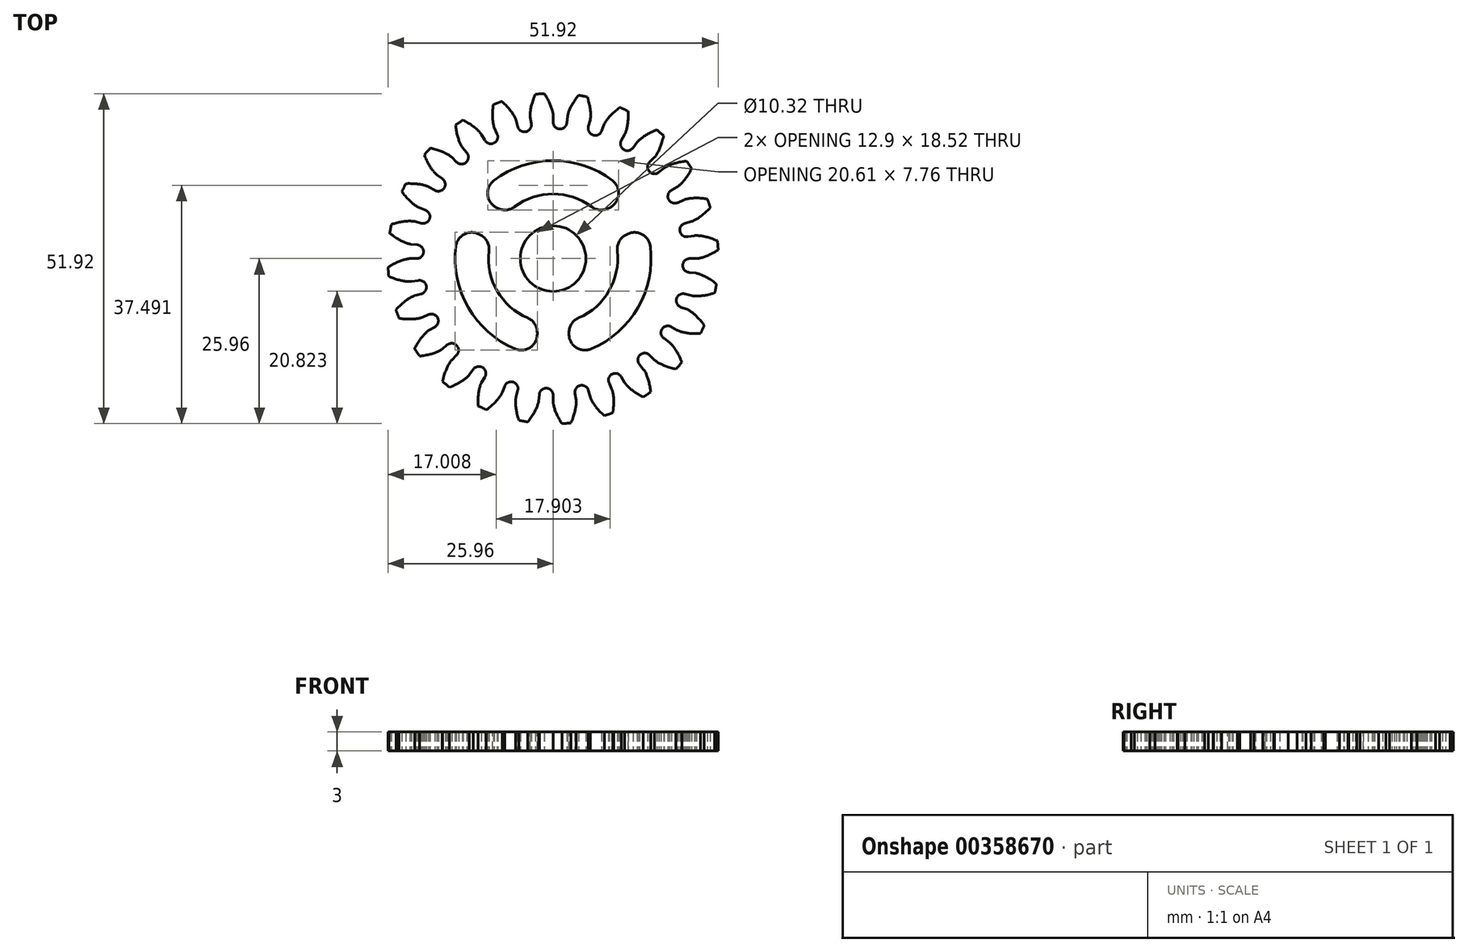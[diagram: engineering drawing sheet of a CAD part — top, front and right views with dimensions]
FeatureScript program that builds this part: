
annotation { "Feature Type Name" : "Feature", "Feature Type Description" : "" }
export const myFeature = defineFeature(function(context is Context, id is Id, definition is map)
    precondition{}
    {
        {
            assignVariable(context, id + "F0", {"name" : "T", "anyValue" : 24});
        }
        {
            assignVariable(context, id + "F1", {"name" : "SP", "anyValue" : 3});
        }
        {
            assignVariable(context, id + "F2", {"name" : "SF", "anyValue" : 2.5});
        }
        {
            var Q0;
            Q0=qCreatedBy(makeId("Top.planeOp"),FACE);
            var sketch = newSketch(context, id + "F3", { "sketchPlane" : qUnion([Q0])});
            skCircle(sketch, "E0", {"center": v(0, 0) * mm, "radius": 26 * mm});
            skCircle(sketch, "E1", {"center": v(0, 0) * mm, "radius": 24 * mm, "construction": true});
            skCircle(sketch, "E2", {"center": v(0, 0) * mm, "radius": 22.55 * mm, "construction": true});
            skCircle(sketch, "E3", {"center": v(0, 0) * mm, "radius": 21.5 * mm});
            skLineSegment(sketch, "E4", {"start": v(0, 0) * mm, "end": v(22.55, 0) * mm});
            skFitSpline(sketch, "E5", {"points": [v(22.55, 0) * mm, v(22.6, 0) * mm, v(22.72, 0.01) * mm, v(22.92, 0.04) * mm, v(23.2, 0.1) * mm, v(23.55, 0.2) * mm, v(23.98, 0.35) * mm, v(24.47, 0.55) * mm, v(25.02, 0.82) * mm, v(25.63, 1.16) * mm, v(26.28, 1.58) * mm], "startDerivative": vector(3.67, 0.15) * mm, "endDerivative": vector(13.44, 8.67) * mm});
            skLineSegment(sketch, "E6", {"start": v(0, 0) * mm, "end": v(25.97, -1.31) * mm, "construction": true});
            skLineSegment(sketch, "E7", {"start": v(0, 0) * mm, "end": v(24, 0.36) * mm, "construction": true});
            skFitSpline(sketch, "E8.MirrorCS", {"points": [v(22.44, -2.28) * mm, v(22.48, -2.28) * mm, v(22.6, -2.3) * mm, v(22.8, -2.36) * mm, v(23.07, -2.44) * mm, v(23.41, -2.58) * mm, v(23.82, -2.77) * mm, v(24.29, -3.02) * mm, v(24.81, -3.34) * mm, v(25.38, -3.74) * mm, v(25.99, -4.23) * mm], "startDerivative": vector(3.63, -0.52) * mm, "endDerivative": vector(12.5, -9.98) * mm});
            skLineSegment(sketch, "E9", {"start": v(0, 0) * mm, "end": v(22.44, -2.28) * mm});
            skSolve(sketch);
        }
        {
            var Q0;
            Q0=qCreatedBy(makeId("Top.planeOp"),FACE);
            var sketch = newSketch(context, id + "F4", { "sketchPlane" : qUnion([Q0])});
            skCircle(sketch, "E10", {"center": v(0, 0) * mm, "radius": 26 * mm});
            skSolve(sketch);
        }
        {
            var Q0;
            {var subQ0=sQuery(id+"F3.wireOp",EDGE,"E5");var subQ7=sQuery(id+"F3.wireOp",EDGE,"E0");var subQ8=makeQuery(id+"F3.imprint","INTERSECT",VERTEX,{"derivedFrom":[subQ7,subQ0]});Q0=makeQuery(id+"F3.imprint","IMPRINT",FACE,{"disambiguationData":[TD([[makeQuery(id+"F3.imprint","IMPRINT",EDGE,{"disambiguationData":[TD([[subQ8,1.0]])],"derivedFrom":subQ7}),1.0]])]});}
            extrude(context, id + "F5", {"entities" : qUnion([Q0]), "depth" : 6 * mm});
        }
        {
            var Q0;
            Q0=makeQuery(id+"F5.opExtrude","CAP_FACE",FACE,{"disambiguationData":[OSD([sQuery(id+"F3.wireOp",EDGE,"E0"),sQuery(id+"F3.wireOp",EDGE,"E3"),sQuery(id+"F3.wireOp",EDGE,"E4"),sQuery(id+"F3.wireOp",EDGE,"E5"),sQuery(id+"F3.wireOp",EDGE,"E8.MirrorCS"),sQuery(id+"F3.wireOp",EDGE,"E9")])],"isStart":true});
            var sketch = newSketch(context, id + "F6", { "sketchPlane" : qUnion([Q0])});
            skCircle(sketch, "E11", {"center": v(21.47, 1.09) * mm, "radius": 1.09 * mm});
            skSolve(sketch);
        }
        {
            var Q0;
            {var subQ1=makeQuery(id+"F5.opExtrude","CAP_EDGE",EDGE,{"disambiguationData":[OSD([sQuery(id+"F3.wireOp",EDGE,"E3")])],"isStart":true});Q0=makeQuery(id+"F6.imprint","IMPRINT",FACE,{"disambiguationData":[TD([[makeQuery(id+"F6.imprint","IMPRINT",EDGE,{"derivedFrom":subQ1}),-1.0]])]});}
            extrude(context, id + "F7", {"entities" : qUnion([Q0]), "operationType" : NewBodyOperationType.ADD, "oppositeDirection" : true, "depth" : 6 * mm});
        }
        {
            var Q0;
            Q0=makeQuery(id+"F4.imprint","IMPRINT",FACE,{"disambiguationData":[TD([[makeQuery(id+"F4.imprint","IMPRINT",EDGE,{"derivedFrom":sQuery(id+"F4.wireOp",EDGE,"E10")}),1.0]])]});
            extrude(context, id + "F8", {"entities" : qUnion([Q0]), "depth" : 3 * mm, "offsetDistance" : 25 * mm});
        }
        {
            var Q0;
            Q0=makeQuery(id+"F5.opExtrude","SWEPT_BODY",BODY,{"disambiguationData":[OSD([sQuery(id+"F3.wireOp",EDGE,"E0"),sQuery(id+"F3.wireOp",EDGE,"E3"),sQuery(id+"F3.wireOp",EDGE,"E4"),sQuery(id+"F3.wireOp",EDGE,"E5"),sQuery(id+"F3.wireOp",EDGE,"E8.MirrorCS"),sQuery(id+"F3.wireOp",EDGE,"E9")])]});
            var Q1;
            Q1=makeQuery(id+"F8.opExtrude","CAP_EDGE",EDGE,{"disambiguationData":[OSD([sQuery(id+"F4.wireOp",EDGE,"E10")])],"isStart":false});
            circularPattern(context, id + "F9", {"entities" : qUnion([Q0]), "axis" : qUnion([Q1]), "angle" : 360 * degree, "instanceCount" : getVariable(context, 'T'), "equalSpace" : true});
        }
        {
            var Q0;
            Q0=makeQuery(id+"F9.opPattern","COPY",BODY,{"derivedFrom":makeQuery(id+"F5.opExtrude","SWEPT_BODY",BODY,{"disambiguationData":[OSD([sQuery(id+"F3.wireOp",EDGE,"E0"),sQuery(id+"F3.wireOp",EDGE,"E3"),sQuery(id+"F3.wireOp",EDGE,"E4"),sQuery(id+"F3.wireOp",EDGE,"E5"),sQuery(id+"F3.wireOp",EDGE,"E8.MirrorCS"),sQuery(id+"F3.wireOp",EDGE,"E9")])]}),"instanceName":"5"});
            var Q1;
            Q1=makeQuery(id+"F9.opPattern","COPY",BODY,{"derivedFrom":makeQuery(id+"F5.opExtrude","SWEPT_BODY",BODY,{"disambiguationData":[OSD([sQuery(id+"F3.wireOp",EDGE,"E0"),sQuery(id+"F3.wireOp",EDGE,"E3"),sQuery(id+"F3.wireOp",EDGE,"E4"),sQuery(id+"F3.wireOp",EDGE,"E5"),sQuery(id+"F3.wireOp",EDGE,"E8.MirrorCS"),sQuery(id+"F3.wireOp",EDGE,"E9")])]}),"instanceName":"6"});
            var Q2;
            Q2=makeQuery(id+"F9.opPattern","COPY",BODY,{"derivedFrom":makeQuery(id+"F5.opExtrude","SWEPT_BODY",BODY,{"disambiguationData":[OSD([sQuery(id+"F3.wireOp",EDGE,"E0"),sQuery(id+"F3.wireOp",EDGE,"E3"),sQuery(id+"F3.wireOp",EDGE,"E4"),sQuery(id+"F3.wireOp",EDGE,"E5"),sQuery(id+"F3.wireOp",EDGE,"E8.MirrorCS"),sQuery(id+"F3.wireOp",EDGE,"E9")])]}),"instanceName":"7"});
            var Q3;
            Q3=makeQuery(id+"F9.opPattern","COPY",BODY,{"derivedFrom":makeQuery(id+"F5.opExtrude","SWEPT_BODY",BODY,{"disambiguationData":[OSD([sQuery(id+"F3.wireOp",EDGE,"E0"),sQuery(id+"F3.wireOp",EDGE,"E3"),sQuery(id+"F3.wireOp",EDGE,"E4"),sQuery(id+"F3.wireOp",EDGE,"E5"),sQuery(id+"F3.wireOp",EDGE,"E8.MirrorCS"),sQuery(id+"F3.wireOp",EDGE,"E9")])]}),"instanceName":"8"});
            var Q4;
            Q4=makeQuery(id+"F9.opPattern","COPY",BODY,{"derivedFrom":makeQuery(id+"F5.opExtrude","SWEPT_BODY",BODY,{"disambiguationData":[OSD([sQuery(id+"F3.wireOp",EDGE,"E0"),sQuery(id+"F3.wireOp",EDGE,"E3"),sQuery(id+"F3.wireOp",EDGE,"E4"),sQuery(id+"F3.wireOp",EDGE,"E5"),sQuery(id+"F3.wireOp",EDGE,"E8.MirrorCS"),sQuery(id+"F3.wireOp",EDGE,"E9")])]}),"instanceName":"9"});
            var Q5;
            Q5=makeQuery(id+"F9.opPattern","COPY",BODY,{"derivedFrom":makeQuery(id+"F5.opExtrude","SWEPT_BODY",BODY,{"disambiguationData":[OSD([sQuery(id+"F3.wireOp",EDGE,"E0"),sQuery(id+"F3.wireOp",EDGE,"E3"),sQuery(id+"F3.wireOp",EDGE,"E4"),sQuery(id+"F3.wireOp",EDGE,"E5"),sQuery(id+"F3.wireOp",EDGE,"E8.MirrorCS"),sQuery(id+"F3.wireOp",EDGE,"E9")])]}),"instanceName":"10"});
            var Q6;
            Q6=makeQuery(id+"F9.opPattern","COPY",BODY,{"derivedFrom":makeQuery(id+"F5.opExtrude","SWEPT_BODY",BODY,{"disambiguationData":[OSD([sQuery(id+"F3.wireOp",EDGE,"E0"),sQuery(id+"F3.wireOp",EDGE,"E3"),sQuery(id+"F3.wireOp",EDGE,"E4"),sQuery(id+"F3.wireOp",EDGE,"E5"),sQuery(id+"F3.wireOp",EDGE,"E8.MirrorCS"),sQuery(id+"F3.wireOp",EDGE,"E9")])]}),"instanceName":"11"});
            var Q7;
            Q7=makeQuery(id+"F9.opPattern","COPY",BODY,{"derivedFrom":makeQuery(id+"F5.opExtrude","SWEPT_BODY",BODY,{"disambiguationData":[OSD([sQuery(id+"F3.wireOp",EDGE,"E0"),sQuery(id+"F3.wireOp",EDGE,"E3"),sQuery(id+"F3.wireOp",EDGE,"E4"),sQuery(id+"F3.wireOp",EDGE,"E5"),sQuery(id+"F3.wireOp",EDGE,"E8.MirrorCS"),sQuery(id+"F3.wireOp",EDGE,"E9")])]}),"instanceName":"12"});
            var Q8;
            Q8=makeQuery(id+"F9.opPattern","COPY",BODY,{"derivedFrom":makeQuery(id+"F5.opExtrude","SWEPT_BODY",BODY,{"disambiguationData":[OSD([sQuery(id+"F3.wireOp",EDGE,"E0"),sQuery(id+"F3.wireOp",EDGE,"E3"),sQuery(id+"F3.wireOp",EDGE,"E4"),sQuery(id+"F3.wireOp",EDGE,"E5"),sQuery(id+"F3.wireOp",EDGE,"E8.MirrorCS"),sQuery(id+"F3.wireOp",EDGE,"E9")])]}),"instanceName":"13"});
            var Q9;
            Q9=makeQuery(id+"F9.opPattern","COPY",BODY,{"derivedFrom":makeQuery(id+"F5.opExtrude","SWEPT_BODY",BODY,{"disambiguationData":[OSD([sQuery(id+"F3.wireOp",EDGE,"E0"),sQuery(id+"F3.wireOp",EDGE,"E3"),sQuery(id+"F3.wireOp",EDGE,"E4"),sQuery(id+"F3.wireOp",EDGE,"E5"),sQuery(id+"F3.wireOp",EDGE,"E8.MirrorCS"),sQuery(id+"F3.wireOp",EDGE,"E9")])]}),"instanceName":"14"});
            var Q10;
            Q10=makeQuery(id+"F9.opPattern","COPY",BODY,{"derivedFrom":makeQuery(id+"F5.opExtrude","SWEPT_BODY",BODY,{"disambiguationData":[OSD([sQuery(id+"F3.wireOp",EDGE,"E0"),sQuery(id+"F3.wireOp",EDGE,"E3"),sQuery(id+"F3.wireOp",EDGE,"E4"),sQuery(id+"F3.wireOp",EDGE,"E5"),sQuery(id+"F3.wireOp",EDGE,"E8.MirrorCS"),sQuery(id+"F3.wireOp",EDGE,"E9")])]}),"instanceName":"15"});
            var Q11;
            Q11=makeQuery(id+"F9.opPattern","COPY",BODY,{"derivedFrom":makeQuery(id+"F5.opExtrude","SWEPT_BODY",BODY,{"disambiguationData":[OSD([sQuery(id+"F3.wireOp",EDGE,"E0"),sQuery(id+"F3.wireOp",EDGE,"E3"),sQuery(id+"F3.wireOp",EDGE,"E4"),sQuery(id+"F3.wireOp",EDGE,"E5"),sQuery(id+"F3.wireOp",EDGE,"E8.MirrorCS"),sQuery(id+"F3.wireOp",EDGE,"E9")])]}),"instanceName":"16"});
            var Q12;
            Q12=makeQuery(id+"F9.opPattern","COPY",BODY,{"derivedFrom":makeQuery(id+"F5.opExtrude","SWEPT_BODY",BODY,{"disambiguationData":[OSD([sQuery(id+"F3.wireOp",EDGE,"E0"),sQuery(id+"F3.wireOp",EDGE,"E3"),sQuery(id+"F3.wireOp",EDGE,"E4"),sQuery(id+"F3.wireOp",EDGE,"E5"),sQuery(id+"F3.wireOp",EDGE,"E8.MirrorCS"),sQuery(id+"F3.wireOp",EDGE,"E9")])]}),"instanceName":"17"});
            var Q13;
            Q13=makeQuery(id+"F9.opPattern","COPY",BODY,{"derivedFrom":makeQuery(id+"F5.opExtrude","SWEPT_BODY",BODY,{"disambiguationData":[OSD([sQuery(id+"F3.wireOp",EDGE,"E0"),sQuery(id+"F3.wireOp",EDGE,"E3"),sQuery(id+"F3.wireOp",EDGE,"E4"),sQuery(id+"F3.wireOp",EDGE,"E5"),sQuery(id+"F3.wireOp",EDGE,"E8.MirrorCS"),sQuery(id+"F3.wireOp",EDGE,"E9")])]}),"instanceName":"18"});
            var Q14;
            Q14=makeQuery(id+"F9.opPattern","COPY",BODY,{"derivedFrom":makeQuery(id+"F5.opExtrude","SWEPT_BODY",BODY,{"disambiguationData":[OSD([sQuery(id+"F3.wireOp",EDGE,"E0"),sQuery(id+"F3.wireOp",EDGE,"E3"),sQuery(id+"F3.wireOp",EDGE,"E4"),sQuery(id+"F3.wireOp",EDGE,"E5"),sQuery(id+"F3.wireOp",EDGE,"E8.MirrorCS"),sQuery(id+"F3.wireOp",EDGE,"E9")])]}),"instanceName":"19"});
            var Q15;
            Q15=makeQuery(id+"F9.opPattern","COPY",BODY,{"derivedFrom":makeQuery(id+"F5.opExtrude","SWEPT_BODY",BODY,{"disambiguationData":[OSD([sQuery(id+"F3.wireOp",EDGE,"E0"),sQuery(id+"F3.wireOp",EDGE,"E3"),sQuery(id+"F3.wireOp",EDGE,"E4"),sQuery(id+"F3.wireOp",EDGE,"E5"),sQuery(id+"F3.wireOp",EDGE,"E8.MirrorCS"),sQuery(id+"F3.wireOp",EDGE,"E9")])]}),"instanceName":"20"});
            var Q16;
            Q16=makeQuery(id+"F9.opPattern","COPY",BODY,{"derivedFrom":makeQuery(id+"F5.opExtrude","SWEPT_BODY",BODY,{"disambiguationData":[OSD([sQuery(id+"F3.wireOp",EDGE,"E0"),sQuery(id+"F3.wireOp",EDGE,"E3"),sQuery(id+"F3.wireOp",EDGE,"E4"),sQuery(id+"F3.wireOp",EDGE,"E5"),sQuery(id+"F3.wireOp",EDGE,"E8.MirrorCS"),sQuery(id+"F3.wireOp",EDGE,"E9")])]}),"instanceName":"21"});
            var Q17;
            Q17=makeQuery(id+"F9.opPattern","COPY",BODY,{"derivedFrom":makeQuery(id+"F5.opExtrude","SWEPT_BODY",BODY,{"disambiguationData":[OSD([sQuery(id+"F3.wireOp",EDGE,"E0"),sQuery(id+"F3.wireOp",EDGE,"E3"),sQuery(id+"F3.wireOp",EDGE,"E4"),sQuery(id+"F3.wireOp",EDGE,"E5"),sQuery(id+"F3.wireOp",EDGE,"E8.MirrorCS"),sQuery(id+"F3.wireOp",EDGE,"E9")])]}),"instanceName":"22"});
            var Q18;
            Q18=makeQuery(id+"F9.opPattern","COPY",BODY,{"derivedFrom":makeQuery(id+"F5.opExtrude","SWEPT_BODY",BODY,{"disambiguationData":[OSD([sQuery(id+"F3.wireOp",EDGE,"E0"),sQuery(id+"F3.wireOp",EDGE,"E3"),sQuery(id+"F3.wireOp",EDGE,"E4"),sQuery(id+"F3.wireOp",EDGE,"E5"),sQuery(id+"F3.wireOp",EDGE,"E8.MirrorCS"),sQuery(id+"F3.wireOp",EDGE,"E9")])]}),"instanceName":"23"});
            var Q19;
            Q19=makeQuery(id+"F9.opPattern","COPY",BODY,{"derivedFrom":makeQuery(id+"F5.opExtrude","SWEPT_BODY",BODY,{"disambiguationData":[OSD([sQuery(id+"F3.wireOp",EDGE,"E0"),sQuery(id+"F3.wireOp",EDGE,"E3"),sQuery(id+"F3.wireOp",EDGE,"E4"),sQuery(id+"F3.wireOp",EDGE,"E5"),sQuery(id+"F3.wireOp",EDGE,"E8.MirrorCS"),sQuery(id+"F3.wireOp",EDGE,"E9")])]}),"instanceName":"24"});
            var Q20;
            Q20=makeQuery(id+"F9.opPattern","COPY",BODY,{"derivedFrom":makeQuery(id+"F5.opExtrude","SWEPT_BODY",BODY,{"disambiguationData":[OSD([sQuery(id+"F3.wireOp",EDGE,"E0"),sQuery(id+"F3.wireOp",EDGE,"E3"),sQuery(id+"F3.wireOp",EDGE,"E4"),sQuery(id+"F3.wireOp",EDGE,"E5"),sQuery(id+"F3.wireOp",EDGE,"E8.MirrorCS"),sQuery(id+"F3.wireOp",EDGE,"E9")])]}),"instanceName":"25"});
            var Q21;
            Q21=makeQuery(id+"F9.opPattern","COPY",BODY,{"derivedFrom":makeQuery(id+"F5.opExtrude","SWEPT_BODY",BODY,{"disambiguationData":[OSD([sQuery(id+"F3.wireOp",EDGE,"E0"),sQuery(id+"F3.wireOp",EDGE,"E3"),sQuery(id+"F3.wireOp",EDGE,"E4"),sQuery(id+"F3.wireOp",EDGE,"E5"),sQuery(id+"F3.wireOp",EDGE,"E8.MirrorCS"),sQuery(id+"F3.wireOp",EDGE,"E9")])]}),"instanceName":"26"});
            var Q22;
            Q22=makeQuery(id+"F9.opPattern","COPY",BODY,{"derivedFrom":makeQuery(id+"F5.opExtrude","SWEPT_BODY",BODY,{"disambiguationData":[OSD([sQuery(id+"F3.wireOp",EDGE,"E0"),sQuery(id+"F3.wireOp",EDGE,"E3"),sQuery(id+"F3.wireOp",EDGE,"E4"),sQuery(id+"F3.wireOp",EDGE,"E5"),sQuery(id+"F3.wireOp",EDGE,"E8.MirrorCS"),sQuery(id+"F3.wireOp",EDGE,"E9")])]}),"instanceName":"27"});
            var Q23;
            Q23=makeQuery(id+"F9.opPattern","COPY",BODY,{"derivedFrom":makeQuery(id+"F5.opExtrude","SWEPT_BODY",BODY,{"disambiguationData":[OSD([sQuery(id+"F3.wireOp",EDGE,"E0"),sQuery(id+"F3.wireOp",EDGE,"E3"),sQuery(id+"F3.wireOp",EDGE,"E4"),sQuery(id+"F3.wireOp",EDGE,"E5"),sQuery(id+"F3.wireOp",EDGE,"E8.MirrorCS"),sQuery(id+"F3.wireOp",EDGE,"E9")])]}),"instanceName":"28"});
            var Q24;
            Q24=makeQuery(id+"F9.opPattern","COPY",BODY,{"derivedFrom":makeQuery(id+"F5.opExtrude","SWEPT_BODY",BODY,{"disambiguationData":[OSD([sQuery(id+"F3.wireOp",EDGE,"E0"),sQuery(id+"F3.wireOp",EDGE,"E3"),sQuery(id+"F3.wireOp",EDGE,"E4"),sQuery(id+"F3.wireOp",EDGE,"E5"),sQuery(id+"F3.wireOp",EDGE,"E8.MirrorCS"),sQuery(id+"F3.wireOp",EDGE,"E9")])]}),"instanceName":"29"});
            var Q25;
            Q25=makeQuery(id+"F5.opExtrude","SWEPT_BODY",BODY,{"disambiguationData":[OSD([sQuery(id+"F3.wireOp",EDGE,"E0"),sQuery(id+"F3.wireOp",EDGE,"E3"),sQuery(id+"F3.wireOp",EDGE,"E4"),sQuery(id+"F3.wireOp",EDGE,"E5"),sQuery(id+"F3.wireOp",EDGE,"E8.MirrorCS"),sQuery(id+"F3.wireOp",EDGE,"E9")])]});
            var Q26;
            Q26=makeQuery(id+"F9.opPattern","COPY",BODY,{"derivedFrom":makeQuery(id+"F5.opExtrude","SWEPT_BODY",BODY,{"disambiguationData":[OSD([sQuery(id+"F3.wireOp",EDGE,"E0"),sQuery(id+"F3.wireOp",EDGE,"E3"),sQuery(id+"F3.wireOp",EDGE,"E4"),sQuery(id+"F3.wireOp",EDGE,"E5"),sQuery(id+"F3.wireOp",EDGE,"E8.MirrorCS"),sQuery(id+"F3.wireOp",EDGE,"E9")])]}),"instanceName":"1"});
            var Q27;
            Q27=makeQuery(id+"F9.opPattern","COPY",BODY,{"derivedFrom":makeQuery(id+"F5.opExtrude","SWEPT_BODY",BODY,{"disambiguationData":[OSD([sQuery(id+"F3.wireOp",EDGE,"E0"),sQuery(id+"F3.wireOp",EDGE,"E3"),sQuery(id+"F3.wireOp",EDGE,"E4"),sQuery(id+"F3.wireOp",EDGE,"E5"),sQuery(id+"F3.wireOp",EDGE,"E8.MirrorCS"),sQuery(id+"F3.wireOp",EDGE,"E9")])]}),"instanceName":"2"});
            var Q28;
            Q28=makeQuery(id+"F9.opPattern","COPY",BODY,{"derivedFrom":makeQuery(id+"F5.opExtrude","SWEPT_BODY",BODY,{"disambiguationData":[OSD([sQuery(id+"F3.wireOp",EDGE,"E0"),sQuery(id+"F3.wireOp",EDGE,"E3"),sQuery(id+"F3.wireOp",EDGE,"E4"),sQuery(id+"F3.wireOp",EDGE,"E5"),sQuery(id+"F3.wireOp",EDGE,"E8.MirrorCS"),sQuery(id+"F3.wireOp",EDGE,"E9")])]}),"instanceName":"3"});
            var Q29;
            Q29=makeQuery(id+"F9.opPattern","COPY",BODY,{"derivedFrom":makeQuery(id+"F5.opExtrude","SWEPT_BODY",BODY,{"disambiguationData":[OSD([sQuery(id+"F3.wireOp",EDGE,"E0"),sQuery(id+"F3.wireOp",EDGE,"E3"),sQuery(id+"F3.wireOp",EDGE,"E4"),sQuery(id+"F3.wireOp",EDGE,"E5"),sQuery(id+"F3.wireOp",EDGE,"E8.MirrorCS"),sQuery(id+"F3.wireOp",EDGE,"E9")])]}),"instanceName":"4"});
            var Q30;
            Q30=makeQuery(id+"F9.opPattern","COPY",BODY,{"derivedFrom":makeQuery(id+"F5.opExtrude","SWEPT_BODY",BODY,{"disambiguationData":[OSD([sQuery(id+"F3.wireOp",EDGE,"E0"),sQuery(id+"F3.wireOp",EDGE,"E3"),sQuery(id+"F3.wireOp",EDGE,"E5"),sQuery(id+"F3.wireOp",EDGE,"E8.MirrorCS")])]}),"instanceName":"30"});
            var Q31;
            Q31=makeQuery(id+"F9.opPattern","COPY",BODY,{"derivedFrom":makeQuery(id+"F5.opExtrude","SWEPT_BODY",BODY,{"disambiguationData":[OSD([sQuery(id+"F3.wireOp",EDGE,"E0"),sQuery(id+"F3.wireOp",EDGE,"E3"),sQuery(id+"F3.wireOp",EDGE,"E5"),sQuery(id+"F3.wireOp",EDGE,"E8.MirrorCS")])]}),"instanceName":"31"});
            var Q32;
            Q32=makeQuery(id+"F9.opPattern","COPY",BODY,{"derivedFrom":makeQuery(id+"F5.opExtrude","SWEPT_BODY",BODY,{"disambiguationData":[OSD([sQuery(id+"F3.wireOp",EDGE,"E0"),sQuery(id+"F3.wireOp",EDGE,"E3"),sQuery(id+"F3.wireOp",EDGE,"E5"),sQuery(id+"F3.wireOp",EDGE,"E8.MirrorCS")])]}),"instanceName":"32"});
            var Q33;
            Q33=makeQuery(id+"F9.opPattern","COPY",BODY,{"derivedFrom":makeQuery(id+"F5.opExtrude","SWEPT_BODY",BODY,{"disambiguationData":[OSD([sQuery(id+"F3.wireOp",EDGE,"E0"),sQuery(id+"F3.wireOp",EDGE,"E3"),sQuery(id+"F3.wireOp",EDGE,"E5"),sQuery(id+"F3.wireOp",EDGE,"E8.MirrorCS")])]}),"instanceName":"33"});
            var Q34;
            Q34=makeQuery(id+"F9.opPattern","COPY",BODY,{"derivedFrom":makeQuery(id+"F5.opExtrude","SWEPT_BODY",BODY,{"disambiguationData":[OSD([sQuery(id+"F3.wireOp",EDGE,"E0"),sQuery(id+"F3.wireOp",EDGE,"E3"),sQuery(id+"F3.wireOp",EDGE,"E5"),sQuery(id+"F3.wireOp",EDGE,"E8.MirrorCS")])]}),"instanceName":"34"});
            var Q35;
            Q35=makeQuery(id+"F9.opPattern","COPY",BODY,{"derivedFrom":makeQuery(id+"F5.opExtrude","SWEPT_BODY",BODY,{"disambiguationData":[OSD([sQuery(id+"F3.wireOp",EDGE,"E0"),sQuery(id+"F3.wireOp",EDGE,"E3"),sQuery(id+"F3.wireOp",EDGE,"E5"),sQuery(id+"F3.wireOp",EDGE,"E8.MirrorCS")])]}),"instanceName":"35"});
            var Q36;
            Q36=makeQuery(id+"F9.opPattern","COPY",BODY,{"derivedFrom":makeQuery(id+"F5.opExtrude","SWEPT_BODY",BODY,{"disambiguationData":[OSD([sQuery(id+"F3.wireOp",EDGE,"E0"),sQuery(id+"F3.wireOp",EDGE,"E3"),sQuery(id+"F3.wireOp",EDGE,"E5"),sQuery(id+"F3.wireOp",EDGE,"E8.MirrorCS")])]}),"instanceName":"36"});
            var Q37;
            Q37=makeQuery(id+"F9.opPattern","COPY",BODY,{"derivedFrom":makeQuery(id+"F5.opExtrude","SWEPT_BODY",BODY,{"disambiguationData":[OSD([sQuery(id+"F3.wireOp",EDGE,"E0"),sQuery(id+"F3.wireOp",EDGE,"E3"),sQuery(id+"F3.wireOp",EDGE,"E5"),sQuery(id+"F3.wireOp",EDGE,"E8.MirrorCS")])]}),"instanceName":"37"});
            var Q38;
            Q38=makeQuery(id+"F9.opPattern","COPY",BODY,{"derivedFrom":makeQuery(id+"F5.opExtrude","SWEPT_BODY",BODY,{"disambiguationData":[OSD([sQuery(id+"F3.wireOp",EDGE,"E0"),sQuery(id+"F3.wireOp",EDGE,"E3"),sQuery(id+"F3.wireOp",EDGE,"E5"),sQuery(id+"F3.wireOp",EDGE,"E8.MirrorCS")])]}),"instanceName":"38"});
            var Q39;
            Q39=makeQuery(id+"F9.opPattern","COPY",BODY,{"derivedFrom":makeQuery(id+"F5.opExtrude","SWEPT_BODY",BODY,{"disambiguationData":[OSD([sQuery(id+"F3.wireOp",EDGE,"E0"),sQuery(id+"F3.wireOp",EDGE,"E3"),sQuery(id+"F3.wireOp",EDGE,"E5"),sQuery(id+"F3.wireOp",EDGE,"E8.MirrorCS")])]}),"instanceName":"39"});
            var Q40;
            Q40=makeQuery(id+"F9.opPattern","COPY",BODY,{"derivedFrom":makeQuery(id+"F5.opExtrude","SWEPT_BODY",BODY,{"disambiguationData":[OSD([sQuery(id+"F3.wireOp",EDGE,"E0"),sQuery(id+"F3.wireOp",EDGE,"E3"),sQuery(id+"F3.wireOp",EDGE,"E5"),sQuery(id+"F3.wireOp",EDGE,"E8.MirrorCS")])]}),"instanceName":"40"});
            var Q41;
            Q41=makeQuery(id+"F9.opPattern","COPY",BODY,{"derivedFrom":makeQuery(id+"F5.opExtrude","SWEPT_BODY",BODY,{"disambiguationData":[OSD([sQuery(id+"F3.wireOp",EDGE,"E0"),sQuery(id+"F3.wireOp",EDGE,"E3"),sQuery(id+"F3.wireOp",EDGE,"E5"),sQuery(id+"F3.wireOp",EDGE,"E8.MirrorCS")])]}),"instanceName":"41"});
            var Q42;
            Q42=makeQuery(id+"F9.opPattern","COPY",BODY,{"derivedFrom":makeQuery(id+"F5.opExtrude","SWEPT_BODY",BODY,{"disambiguationData":[OSD([sQuery(id+"F3.wireOp",EDGE,"E0"),sQuery(id+"F3.wireOp",EDGE,"E3"),sQuery(id+"F3.wireOp",EDGE,"E5"),sQuery(id+"F3.wireOp",EDGE,"E8.MirrorCS")])]}),"instanceName":"42"});
            var Q43;
            Q43=makeQuery(id+"F9.opPattern","COPY",BODY,{"derivedFrom":makeQuery(id+"F5.opExtrude","SWEPT_BODY",BODY,{"disambiguationData":[OSD([sQuery(id+"F3.wireOp",EDGE,"E0"),sQuery(id+"F3.wireOp",EDGE,"E3"),sQuery(id+"F3.wireOp",EDGE,"E5"),sQuery(id+"F3.wireOp",EDGE,"E8.MirrorCS")])]}),"instanceName":"43"});
            var Q44;
            Q44=makeQuery(id+"F9.opPattern","COPY",BODY,{"derivedFrom":makeQuery(id+"F5.opExtrude","SWEPT_BODY",BODY,{"disambiguationData":[OSD([sQuery(id+"F3.wireOp",EDGE,"E0"),sQuery(id+"F3.wireOp",EDGE,"E3"),sQuery(id+"F3.wireOp",EDGE,"E5"),sQuery(id+"F3.wireOp",EDGE,"E8.MirrorCS")])]}),"instanceName":"44"});
            var Q45;
            Q45=makeQuery(id+"F9.opPattern","COPY",BODY,{"derivedFrom":makeQuery(id+"F5.opExtrude","SWEPT_BODY",BODY,{"disambiguationData":[OSD([sQuery(id+"F3.wireOp",EDGE,"E0"),sQuery(id+"F3.wireOp",EDGE,"E3"),sQuery(id+"F3.wireOp",EDGE,"E5"),sQuery(id+"F3.wireOp",EDGE,"E8.MirrorCS")])]}),"instanceName":"45"});
            var Q46;
            Q46=makeQuery(id+"F9.opPattern","COPY",BODY,{"derivedFrom":makeQuery(id+"F5.opExtrude","SWEPT_BODY",BODY,{"disambiguationData":[OSD([sQuery(id+"F3.wireOp",EDGE,"E0"),sQuery(id+"F3.wireOp",EDGE,"E3"),sQuery(id+"F3.wireOp",EDGE,"E5"),sQuery(id+"F3.wireOp",EDGE,"E8.MirrorCS")])]}),"instanceName":"46"});
            var Q47;
            Q47=makeQuery(id+"F9.opPattern","COPY",BODY,{"derivedFrom":makeQuery(id+"F5.opExtrude","SWEPT_BODY",BODY,{"disambiguationData":[OSD([sQuery(id+"F3.wireOp",EDGE,"E0"),sQuery(id+"F3.wireOp",EDGE,"E3"),sQuery(id+"F3.wireOp",EDGE,"E5"),sQuery(id+"F3.wireOp",EDGE,"E8.MirrorCS")])]}),"instanceName":"47"});
            var Q48;
            Q48=makeQuery(id+"F9.opPattern","COPY",BODY,{"derivedFrom":makeQuery(id+"F5.opExtrude","SWEPT_BODY",BODY,{"disambiguationData":[OSD([sQuery(id+"F3.wireOp",EDGE,"E0"),sQuery(id+"F3.wireOp",EDGE,"E3"),sQuery(id+"F3.wireOp",EDGE,"E5"),sQuery(id+"F3.wireOp",EDGE,"E8.MirrorCS")])]}),"instanceName":"48"});
            var Q49;
            Q49=makeQuery(id+"F9.opPattern","COPY",BODY,{"derivedFrom":makeQuery(id+"F5.opExtrude","SWEPT_BODY",BODY,{"disambiguationData":[OSD([sQuery(id+"F3.wireOp",EDGE,"E0"),sQuery(id+"F3.wireOp",EDGE,"E3"),sQuery(id+"F3.wireOp",EDGE,"E5"),sQuery(id+"F3.wireOp",EDGE,"E8.MirrorCS")])]}),"instanceName":"49"});
            var Q50;
            Q50=makeQuery(id+"F9.opPattern","COPY",BODY,{"derivedFrom":makeQuery(id+"F5.opExtrude","SWEPT_BODY",BODY,{"disambiguationData":[OSD([sQuery(id+"F3.wireOp",EDGE,"E0"),sQuery(id+"F3.wireOp",EDGE,"E3"),sQuery(id+"F3.wireOp",EDGE,"E5"),sQuery(id+"F3.wireOp",EDGE,"E8.MirrorCS")])]}),"instanceName":"50"});
            var Q51;
            Q51=makeQuery(id+"F9.opPattern","COPY",BODY,{"derivedFrom":makeQuery(id+"F5.opExtrude","SWEPT_BODY",BODY,{"disambiguationData":[OSD([sQuery(id+"F3.wireOp",EDGE,"E0"),sQuery(id+"F3.wireOp",EDGE,"E3"),sQuery(id+"F3.wireOp",EDGE,"E5"),sQuery(id+"F3.wireOp",EDGE,"E8.MirrorCS")])]}),"instanceName":"51"});
            var Q52;
            Q52=makeQuery(id+"F9.opPattern","COPY",BODY,{"derivedFrom":makeQuery(id+"F5.opExtrude","SWEPT_BODY",BODY,{"disambiguationData":[OSD([sQuery(id+"F3.wireOp",EDGE,"E0"),sQuery(id+"F3.wireOp",EDGE,"E3"),sQuery(id+"F3.wireOp",EDGE,"E5"),sQuery(id+"F3.wireOp",EDGE,"E8.MirrorCS")])]}),"instanceName":"52"});
            var Q53;
            Q53=makeQuery(id+"F9.opPattern","COPY",BODY,{"derivedFrom":makeQuery(id+"F5.opExtrude","SWEPT_BODY",BODY,{"disambiguationData":[OSD([sQuery(id+"F3.wireOp",EDGE,"E0"),sQuery(id+"F3.wireOp",EDGE,"E3"),sQuery(id+"F3.wireOp",EDGE,"E5"),sQuery(id+"F3.wireOp",EDGE,"E8.MirrorCS")])]}),"instanceName":"53"});
            var Q54;
            Q54=makeQuery(id+"F9.opPattern","COPY",BODY,{"derivedFrom":makeQuery(id+"F5.opExtrude","SWEPT_BODY",BODY,{"disambiguationData":[OSD([sQuery(id+"F3.wireOp",EDGE,"E0"),sQuery(id+"F3.wireOp",EDGE,"E3"),sQuery(id+"F3.wireOp",EDGE,"E5"),sQuery(id+"F3.wireOp",EDGE,"E8.MirrorCS")])]}),"instanceName":"54"});
            var Q55;
            Q55=makeQuery(id+"F9.opPattern","COPY",BODY,{"derivedFrom":makeQuery(id+"F5.opExtrude","SWEPT_BODY",BODY,{"disambiguationData":[OSD([sQuery(id+"F3.wireOp",EDGE,"E0"),sQuery(id+"F3.wireOp",EDGE,"E3"),sQuery(id+"F3.wireOp",EDGE,"E5"),sQuery(id+"F3.wireOp",EDGE,"E8.MirrorCS")])]}),"instanceName":"55"});
            var Q56;
            Q56=makeQuery(id+"F9.opPattern","COPY",BODY,{"derivedFrom":makeQuery(id+"F5.opExtrude","SWEPT_BODY",BODY,{"disambiguationData":[OSD([sQuery(id+"F3.wireOp",EDGE,"E0"),sQuery(id+"F3.wireOp",EDGE,"E3"),sQuery(id+"F3.wireOp",EDGE,"E5"),sQuery(id+"F3.wireOp",EDGE,"E8.MirrorCS")])]}),"instanceName":"56"});
            var Q57;
            Q57=makeQuery(id+"F9.opPattern","COPY",BODY,{"derivedFrom":makeQuery(id+"F5.opExtrude","SWEPT_BODY",BODY,{"disambiguationData":[OSD([sQuery(id+"F3.wireOp",EDGE,"E0"),sQuery(id+"F3.wireOp",EDGE,"E3"),sQuery(id+"F3.wireOp",EDGE,"E5"),sQuery(id+"F3.wireOp",EDGE,"E8.MirrorCS")])]}),"instanceName":"57"});
            var Q58;
            Q58=makeQuery(id+"F9.opPattern","COPY",BODY,{"derivedFrom":makeQuery(id+"F5.opExtrude","SWEPT_BODY",BODY,{"disambiguationData":[OSD([sQuery(id+"F3.wireOp",EDGE,"E0"),sQuery(id+"F3.wireOp",EDGE,"E3"),sQuery(id+"F3.wireOp",EDGE,"E5"),sQuery(id+"F3.wireOp",EDGE,"E8.MirrorCS")])]}),"instanceName":"58"});
            var Q59;
            Q59=makeQuery(id+"F9.opPattern","COPY",BODY,{"derivedFrom":makeQuery(id+"F5.opExtrude","SWEPT_BODY",BODY,{"disambiguationData":[OSD([sQuery(id+"F3.wireOp",EDGE,"E0"),sQuery(id+"F3.wireOp",EDGE,"E3"),sQuery(id+"F3.wireOp",EDGE,"E5"),sQuery(id+"F3.wireOp",EDGE,"E8.MirrorCS")])]}),"instanceName":"59"});
            var Q60;
            Q60=makeQuery(id+"F9.opPattern","COPY",BODY,{"derivedFrom":makeQuery(id+"F5.opExtrude","SWEPT_BODY",BODY,{"disambiguationData":[OSD([sQuery(id+"F3.wireOp",EDGE,"E0"),sQuery(id+"F3.wireOp",EDGE,"E3"),sQuery(id+"F3.wireOp",EDGE,"E5"),sQuery(id+"F3.wireOp",EDGE,"E8.MirrorCS")])]}),"instanceName":"60"});
            var Q61;
            Q61=makeQuery(id+"F9.opPattern","COPY",BODY,{"derivedFrom":makeQuery(id+"F5.opExtrude","SWEPT_BODY",BODY,{"disambiguationData":[OSD([sQuery(id+"F3.wireOp",EDGE,"E0"),sQuery(id+"F3.wireOp",EDGE,"E3"),sQuery(id+"F3.wireOp",EDGE,"E5"),sQuery(id+"F3.wireOp",EDGE,"E8.MirrorCS")])]}),"instanceName":"61"});
            var Q62;
            Q62=makeQuery(id+"F9.opPattern","COPY",BODY,{"derivedFrom":makeQuery(id+"F5.opExtrude","SWEPT_BODY",BODY,{"disambiguationData":[OSD([sQuery(id+"F3.wireOp",EDGE,"E0"),sQuery(id+"F3.wireOp",EDGE,"E3"),sQuery(id+"F3.wireOp",EDGE,"E5"),sQuery(id+"F3.wireOp",EDGE,"E8.MirrorCS")])]}),"instanceName":"62"});
            var Q63;
            Q63=makeQuery(id+"F9.opPattern","COPY",BODY,{"derivedFrom":makeQuery(id+"F5.opExtrude","SWEPT_BODY",BODY,{"disambiguationData":[OSD([sQuery(id+"F3.wireOp",EDGE,"E0"),sQuery(id+"F3.wireOp",EDGE,"E3"),sQuery(id+"F3.wireOp",EDGE,"E5"),sQuery(id+"F3.wireOp",EDGE,"E8.MirrorCS")])]}),"instanceName":"63"});
            var Q64;
            Q64=makeQuery(id+"F9.opPattern","COPY",BODY,{"derivedFrom":makeQuery(id+"F5.opExtrude","SWEPT_BODY",BODY,{"disambiguationData":[OSD([sQuery(id+"F3.wireOp",EDGE,"E0"),sQuery(id+"F3.wireOp",EDGE,"E3"),sQuery(id+"F3.wireOp",EDGE,"E5"),sQuery(id+"F3.wireOp",EDGE,"E8.MirrorCS")])]}),"instanceName":"64"});
            var Q65;
            Q65=makeQuery(id+"F9.opPattern","COPY",BODY,{"derivedFrom":makeQuery(id+"F5.opExtrude","SWEPT_BODY",BODY,{"disambiguationData":[OSD([sQuery(id+"F3.wireOp",EDGE,"E0"),sQuery(id+"F3.wireOp",EDGE,"E3"),sQuery(id+"F3.wireOp",EDGE,"E5"),sQuery(id+"F3.wireOp",EDGE,"E8.MirrorCS")])]}),"instanceName":"65"});
            var Q66;
            Q66=makeQuery(id+"F9.opPattern","COPY",BODY,{"derivedFrom":makeQuery(id+"F5.opExtrude","SWEPT_BODY",BODY,{"disambiguationData":[OSD([sQuery(id+"F3.wireOp",EDGE,"E0"),sQuery(id+"F3.wireOp",EDGE,"E3"),sQuery(id+"F3.wireOp",EDGE,"E5"),sQuery(id+"F3.wireOp",EDGE,"E8.MirrorCS")])]}),"instanceName":"66"});
            var Q67;
            Q67=makeQuery(id+"F9.opPattern","COPY",BODY,{"derivedFrom":makeQuery(id+"F5.opExtrude","SWEPT_BODY",BODY,{"disambiguationData":[OSD([sQuery(id+"F3.wireOp",EDGE,"E0"),sQuery(id+"F3.wireOp",EDGE,"E3"),sQuery(id+"F3.wireOp",EDGE,"E5"),sQuery(id+"F3.wireOp",EDGE,"E8.MirrorCS")])]}),"instanceName":"67"});
            var Q68;
            Q68=makeQuery(id+"F9.opPattern","COPY",BODY,{"derivedFrom":makeQuery(id+"F5.opExtrude","SWEPT_BODY",BODY,{"disambiguationData":[OSD([sQuery(id+"F3.wireOp",EDGE,"E0"),sQuery(id+"F3.wireOp",EDGE,"E3"),sQuery(id+"F3.wireOp",EDGE,"E5"),sQuery(id+"F3.wireOp",EDGE,"E8.MirrorCS")])]}),"instanceName":"68"});
            var Q69;
            Q69=makeQuery(id+"F9.opPattern","COPY",BODY,{"derivedFrom":makeQuery(id+"F5.opExtrude","SWEPT_BODY",BODY,{"disambiguationData":[OSD([sQuery(id+"F3.wireOp",EDGE,"E0"),sQuery(id+"F3.wireOp",EDGE,"E3"),sQuery(id+"F3.wireOp",EDGE,"E5"),sQuery(id+"F3.wireOp",EDGE,"E8.MirrorCS")])]}),"instanceName":"69"});
            var Q70;
            Q70=makeQuery(id+"F9.opPattern","COPY",BODY,{"derivedFrom":makeQuery(id+"F5.opExtrude","SWEPT_BODY",BODY,{"disambiguationData":[OSD([sQuery(id+"F3.wireOp",EDGE,"E0"),sQuery(id+"F3.wireOp",EDGE,"E3"),sQuery(id+"F3.wireOp",EDGE,"E5"),sQuery(id+"F3.wireOp",EDGE,"E8.MirrorCS")])]}),"instanceName":"70"});
            var Q71;
            Q71=makeQuery(id+"F9.opPattern","COPY",BODY,{"derivedFrom":makeQuery(id+"F5.opExtrude","SWEPT_BODY",BODY,{"disambiguationData":[OSD([sQuery(id+"F3.wireOp",EDGE,"E0"),sQuery(id+"F3.wireOp",EDGE,"E3"),sQuery(id+"F3.wireOp",EDGE,"E5"),sQuery(id+"F3.wireOp",EDGE,"E8.MirrorCS")])]}),"instanceName":"71"});
            var Q72;
            Q72=makeQuery(id+"F9.opPattern","COPY",BODY,{"derivedFrom":makeQuery(id+"F5.opExtrude","SWEPT_BODY",BODY,{"disambiguationData":[OSD([sQuery(id+"F3.wireOp",EDGE,"E0"),sQuery(id+"F3.wireOp",EDGE,"E3"),sQuery(id+"F3.wireOp",EDGE,"E5"),sQuery(id+"F3.wireOp",EDGE,"E8.MirrorCS")])]}),"instanceName":"72"});
            var Q73;
            Q73=makeQuery(id+"F9.opPattern","COPY",BODY,{"derivedFrom":makeQuery(id+"F5.opExtrude","SWEPT_BODY",BODY,{"disambiguationData":[OSD([sQuery(id+"F3.wireOp",EDGE,"E0"),sQuery(id+"F3.wireOp",EDGE,"E3"),sQuery(id+"F3.wireOp",EDGE,"E5"),sQuery(id+"F3.wireOp",EDGE,"E8.MirrorCS")])]}),"instanceName":"73"});
            var Q74;
            Q74=makeQuery(id+"F9.opPattern","COPY",BODY,{"derivedFrom":makeQuery(id+"F5.opExtrude","SWEPT_BODY",BODY,{"disambiguationData":[OSD([sQuery(id+"F3.wireOp",EDGE,"E0"),sQuery(id+"F3.wireOp",EDGE,"E3"),sQuery(id+"F3.wireOp",EDGE,"E5"),sQuery(id+"F3.wireOp",EDGE,"E8.MirrorCS")])]}),"instanceName":"74"});
            var Q75;
            Q75=makeQuery(id+"F9.opPattern","COPY",BODY,{"derivedFrom":makeQuery(id+"F5.opExtrude","SWEPT_BODY",BODY,{"disambiguationData":[OSD([sQuery(id+"F3.wireOp",EDGE,"E0"),sQuery(id+"F3.wireOp",EDGE,"E3"),sQuery(id+"F3.wireOp",EDGE,"E5"),sQuery(id+"F3.wireOp",EDGE,"E8.MirrorCS")])]}),"instanceName":"75"});
            var Q76;
            Q76=makeQuery(id+"F9.opPattern","COPY",BODY,{"derivedFrom":makeQuery(id+"F5.opExtrude","SWEPT_BODY",BODY,{"disambiguationData":[OSD([sQuery(id+"F3.wireOp",EDGE,"E0"),sQuery(id+"F3.wireOp",EDGE,"E3"),sQuery(id+"F3.wireOp",EDGE,"E5"),sQuery(id+"F3.wireOp",EDGE,"E8.MirrorCS")])]}),"instanceName":"76"});
            var Q77;
            Q77=makeQuery(id+"F9.opPattern","COPY",BODY,{"derivedFrom":makeQuery(id+"F5.opExtrude","SWEPT_BODY",BODY,{"disambiguationData":[OSD([sQuery(id+"F3.wireOp",EDGE,"E0"),sQuery(id+"F3.wireOp",EDGE,"E3"),sQuery(id+"F3.wireOp",EDGE,"E5"),sQuery(id+"F3.wireOp",EDGE,"E8.MirrorCS")])]}),"instanceName":"77"});
            var Q78;
            Q78=makeQuery(id+"F9.opPattern","COPY",BODY,{"derivedFrom":makeQuery(id+"F5.opExtrude","SWEPT_BODY",BODY,{"disambiguationData":[OSD([sQuery(id+"F3.wireOp",EDGE,"E0"),sQuery(id+"F3.wireOp",EDGE,"E3"),sQuery(id+"F3.wireOp",EDGE,"E5"),sQuery(id+"F3.wireOp",EDGE,"E8.MirrorCS")])]}),"instanceName":"78"});
            var Q79;
            Q79=makeQuery(id+"F9.opPattern","COPY",BODY,{"derivedFrom":makeQuery(id+"F5.opExtrude","SWEPT_BODY",BODY,{"disambiguationData":[OSD([sQuery(id+"F3.wireOp",EDGE,"E0"),sQuery(id+"F3.wireOp",EDGE,"E3"),sQuery(id+"F3.wireOp",EDGE,"E5"),sQuery(id+"F3.wireOp",EDGE,"E8.MirrorCS")])]}),"instanceName":"79"});
            var Q80;
            Q80=makeQuery(id+"F9.opPattern","COPY",BODY,{"derivedFrom":makeQuery(id+"F5.opExtrude","SWEPT_BODY",BODY,{"disambiguationData":[OSD([sQuery(id+"F3.wireOp",EDGE,"E0"),sQuery(id+"F3.wireOp",EDGE,"E3"),sQuery(id+"F3.wireOp",EDGE,"E5"),sQuery(id+"F3.wireOp",EDGE,"E8.MirrorCS")])]}),"instanceName":"80"});
            var Q81;
            Q81=makeQuery(id+"F9.opPattern","COPY",BODY,{"derivedFrom":makeQuery(id+"F5.opExtrude","SWEPT_BODY",BODY,{"disambiguationData":[OSD([sQuery(id+"F3.wireOp",EDGE,"E0"),sQuery(id+"F3.wireOp",EDGE,"E3"),sQuery(id+"F3.wireOp",EDGE,"E5"),sQuery(id+"F3.wireOp",EDGE,"E8.MirrorCS")])]}),"instanceName":"81"});
            var Q82;
            Q82=makeQuery(id+"F9.opPattern","COPY",BODY,{"derivedFrom":makeQuery(id+"F5.opExtrude","SWEPT_BODY",BODY,{"disambiguationData":[OSD([sQuery(id+"F3.wireOp",EDGE,"E0"),sQuery(id+"F3.wireOp",EDGE,"E3"),sQuery(id+"F3.wireOp",EDGE,"E5"),sQuery(id+"F3.wireOp",EDGE,"E8.MirrorCS")])]}),"instanceName":"82"});
            var Q83;
            Q83=makeQuery(id+"F9.opPattern","COPY",BODY,{"derivedFrom":makeQuery(id+"F5.opExtrude","SWEPT_BODY",BODY,{"disambiguationData":[OSD([sQuery(id+"F3.wireOp",EDGE,"E0"),sQuery(id+"F3.wireOp",EDGE,"E3"),sQuery(id+"F3.wireOp",EDGE,"E5"),sQuery(id+"F3.wireOp",EDGE,"E8.MirrorCS")])]}),"instanceName":"83"});
            var Q84;
            Q84=makeQuery(id+"F9.opPattern","COPY",BODY,{"derivedFrom":makeQuery(id+"F5.opExtrude","SWEPT_BODY",BODY,{"disambiguationData":[OSD([sQuery(id+"F3.wireOp",EDGE,"E0"),sQuery(id+"F3.wireOp",EDGE,"E3"),sQuery(id+"F3.wireOp",EDGE,"E5"),sQuery(id+"F3.wireOp",EDGE,"E8.MirrorCS")])]}),"instanceName":"84"});
            var Q85;
            Q85=makeQuery(id+"F9.opPattern","COPY",BODY,{"derivedFrom":makeQuery(id+"F5.opExtrude","SWEPT_BODY",BODY,{"disambiguationData":[OSD([sQuery(id+"F3.wireOp",EDGE,"E0"),sQuery(id+"F3.wireOp",EDGE,"E3"),sQuery(id+"F3.wireOp",EDGE,"E5"),sQuery(id+"F3.wireOp",EDGE,"E8.MirrorCS")])]}),"instanceName":"85"});
            var Q86;
            Q86=makeQuery(id+"F9.opPattern","COPY",BODY,{"derivedFrom":makeQuery(id+"F5.opExtrude","SWEPT_BODY",BODY,{"disambiguationData":[OSD([sQuery(id+"F3.wireOp",EDGE,"E0"),sQuery(id+"F3.wireOp",EDGE,"E3"),sQuery(id+"F3.wireOp",EDGE,"E5"),sQuery(id+"F3.wireOp",EDGE,"E8.MirrorCS")])]}),"instanceName":"86"});
            var Q87;
            Q87=makeQuery(id+"F9.opPattern","COPY",BODY,{"derivedFrom":makeQuery(id+"F5.opExtrude","SWEPT_BODY",BODY,{"disambiguationData":[OSD([sQuery(id+"F3.wireOp",EDGE,"E0"),sQuery(id+"F3.wireOp",EDGE,"E3"),sQuery(id+"F3.wireOp",EDGE,"E5"),sQuery(id+"F3.wireOp",EDGE,"E8.MirrorCS")])]}),"instanceName":"87"});
            var Q88;
            Q88=makeQuery(id+"F9.opPattern","COPY",BODY,{"derivedFrom":makeQuery(id+"F5.opExtrude","SWEPT_BODY",BODY,{"disambiguationData":[OSD([sQuery(id+"F3.wireOp",EDGE,"E0"),sQuery(id+"F3.wireOp",EDGE,"E3"),sQuery(id+"F3.wireOp",EDGE,"E5"),sQuery(id+"F3.wireOp",EDGE,"E8.MirrorCS")])]}),"instanceName":"88"});
            var Q89;
            Q89=makeQuery(id+"F9.opPattern","COPY",BODY,{"derivedFrom":makeQuery(id+"F5.opExtrude","SWEPT_BODY",BODY,{"disambiguationData":[OSD([sQuery(id+"F3.wireOp",EDGE,"E0"),sQuery(id+"F3.wireOp",EDGE,"E3"),sQuery(id+"F3.wireOp",EDGE,"E5"),sQuery(id+"F3.wireOp",EDGE,"E8.MirrorCS")])]}),"instanceName":"89"});
            var Q90;
            Q90=makeQuery(id+"F8.opExtrude","SWEPT_BODY",BODY,{"disambiguationData":[OSD([sQuery(id+"F4.wireOp",EDGE,"E10")])]});
            booleanBodies(context, id + "F10", {"operationType" : BooleanOperationType.SUBTRACTION, "tools" : qUnion([Q0, Q1, Q2, Q3, Q4, Q5, Q6, Q7, Q8, Q9, Q10, Q11, Q12, Q13, Q14, Q15, Q16, Q17, Q18, Q19, Q20, Q21, Q22, Q23, Q24, Q25, Q26, Q27, Q28, Q29, Q30, Q31, Q32, Q33, Q34, Q35, Q36, Q37, Q38, Q39, Q40, Q41, Q42, Q43, Q44, Q45, Q46, Q47, Q48, Q49, Q50, Q51, Q52, Q53, Q54, Q55, Q56, Q57, Q58, Q59, Q60, Q61, Q62, Q63, Q64, Q65, Q66, Q67, Q68, Q69, Q70, Q71, Q72, Q73, Q74, Q75, Q76, Q77, Q78, Q79, Q80, Q81, Q82, Q83, Q84, Q85, Q86, Q87, Q88, Q89]), "targets" : qUnion([Q90])});
        }
        {
            var Q0;
            Q0=makeQuery(id+"F8.opExtrude","CAP_FACE",FACE,{"disambiguationData":[OSD([sQuery(id+"F4.wireOp",EDGE,"E10")])],"isStart":true});
            var sketch = newSketch(context, id + "F11", { "sketchPlane" : qUnion([Q0])});
            skCircle(sketch, "E12", {"center": v(0, 0) * mm, "radius": 5.16 * mm});
            skCircle(sketch, "E13", {"center": v(0, 0) * mm, "radius": 10.16 * mm});
            skCircle(sketch, "E14", {"center": v(0, 0) * mm, "radius": 15.41 * mm});
            skLineSegment(sketch, "E15", {"start": v(0, 0) * mm, "end": v(0, 15.41) * mm, "construction": true});
            skLineSegment(sketch, "E16.0", {"start": v(2.5, 0) * mm, "end": v(2.5, 15.2) * mm});
            skLineSegment(sketch, "E17", {"start": v(0, 0) * mm, "end": v(17.68, -10.2) * mm, "construction": true});
            skLineSegment(sketch, "E18.0", {"start": v(1.25, 2.17) * mm, "end": v(18.8, -7.96) * mm});
            skCircle(sketch, "E19", {"center": v(0, 0) * mm, "radius": 20.41 * mm});
            skSolve(sketch);
        }
        {
            var Q0;
            Q0=makeQuery(id+"F11.imprint","IMPRINT",FACE,{"disambiguationData":[TD([[makeQuery(id+"F11.imprint","IMPRINT",EDGE,{"derivedFrom":sQuery(id+"F11.wireOp",EDGE,"E12")}),1.0]])]});
            extrude(context, id + "F12", {"entities" : qUnion([Q0]), "operationType" : NewBodyOperationType.REMOVE, "oppositeDirection" : true, "depth" : 25 * mm});
        }
        {
            var Q0;
            {var subQ0=sQuery(id+"F11.wireOp",EDGE,"E16.0");var subQ1=sQuery(id+"F11.wireOp",EDGE,"E13");var subQ2=makeQuery(id+"F11.imprint","INTERSECT",VERTEX,{"derivedFrom":[subQ1,subQ0]});Q0=makeQuery(id+"F11.imprint","IMPRINT",FACE,{"disambiguationData":[TD([[makeQuery(id+"F11.imprint","IMPRINT",EDGE,{"disambiguationData":[TD([[subQ2,1.0]])],"derivedFrom":subQ1}),-1.0]])]});}
            extrude(context, id + "F13", {"entities" : qUnion([Q0]), "oppositeDirection" : true, "depth" : 6 * mm});
        }
        {
            var Q0;
            Q0=makeQuery(id+"F13.opExtrude","SWEPT_EDGE",EDGE,{"disambiguationData":[OSD([sQuery(id+"F11.wireOp",EDGE,"E14"),sQuery(id+"F11.wireOp",EDGE,"E16.0")])]});
            var Q1;
            Q1=makeQuery(id+"F13.opExtrude","SWEPT_EDGE",EDGE,{"disambiguationData":[OSD([sQuery(id+"F11.wireOp",EDGE,"E13"),sQuery(id+"F11.wireOp",EDGE,"E16.0")])]});
            var Q2;
            Q2=makeQuery(id+"F13.opExtrude","SWEPT_EDGE",EDGE,{"disambiguationData":[OSD([sQuery(id+"F11.wireOp",EDGE,"E13"),sQuery(id+"F11.wireOp",EDGE,"E18.0")])]});
            var Q3;
            Q3=makeQuery(id+"F13.opExtrude","SWEPT_EDGE",EDGE,{"disambiguationData":[OSD([sQuery(id+"F11.wireOp",EDGE,"E14"),sQuery(id+"F11.wireOp",EDGE,"E18.0")])]});
            fillet(context, id + "F14", {"entities" : qUnion([Q0, Q1, Q2, Q3]), "radius" : (getVariable(context, 'SF')) * mm, "tangentPropagation" : true, "allowEdgeOverflow" : false});
        }
        {
            var Q0;
            Q0=makeQuery(id+"F13.opExtrude","SWEPT_BODY",BODY,{"disambiguationData":[OSD([sQuery(id+"F11.wireOp",EDGE,"E13"),sQuery(id+"F11.wireOp",EDGE,"E14"),sQuery(id+"F11.wireOp",EDGE,"E16.0"),sQuery(id+"F11.wireOp",EDGE,"E18.0")])]});
            var Q1;
            Q1=makeQuery(id+"F12.boolean.opBoolean","INTERSECT",EDGE,{"derivedFrom":[makeQuery(id+"F8.opExtrude","CAP_FACE",FACE,{"disambiguationData":[OSD([sQuery(id+"F4.wireOp",EDGE,"E10")])],"isStart":false}),makeQuery(id+"F12.opExtrude","SWEPT_FACE",FACE,{"disambiguationData":[OSD([sQuery(id+"F11.wireOp",EDGE,"E12")])]})]});
            circularPattern(context, id + "F15", {"entities" : qUnion([Q0]), "axis" : qUnion([Q1]), "angle" : 360 * degree, "instanceCount" : getVariable(context, 'SP'), "equalSpace" : true});
        }
        {
            var Q0;
            Q0=makeQuery(id+"F15.opPattern","COPY",BODY,{"derivedFrom":makeQuery(id+"F13.opExtrude","SWEPT_BODY",BODY,{"disambiguationData":[OSD([sQuery(id+"F11.wireOp",EDGE,"E13"),sQuery(id+"F11.wireOp",EDGE,"E14"),sQuery(id+"F11.wireOp",EDGE,"E16.0"),sQuery(id+"F11.wireOp",EDGE,"E18.0")])]}),"instanceName":"2"});
            var Q1;
            Q1=makeQuery(id+"F15.opPattern","COPY",BODY,{"derivedFrom":makeQuery(id+"F13.opExtrude","SWEPT_BODY",BODY,{"disambiguationData":[OSD([sQuery(id+"F11.wireOp",EDGE,"E13"),sQuery(id+"F11.wireOp",EDGE,"E14"),sQuery(id+"F11.wireOp",EDGE,"E16.0"),sQuery(id+"F11.wireOp",EDGE,"E18.0")])]}),"instanceName":"1"});
            var Q2;
            Q2=makeQuery(id+"F13.opExtrude","SWEPT_BODY",BODY,{"disambiguationData":[OSD([sQuery(id+"F11.wireOp",EDGE,"E13"),sQuery(id+"F11.wireOp",EDGE,"E14"),sQuery(id+"F11.wireOp",EDGE,"E16.0"),sQuery(id+"F11.wireOp",EDGE,"E18.0")])]});
            var Q3;
            Q3=makeQuery(id+"F15.opPattern","COPY",BODY,{"derivedFrom":makeQuery(id+"F13.opExtrude","SWEPT_BODY",BODY,{"disambiguationData":[OSD([sQuery(id+"F11.wireOp",EDGE,"E13"),sQuery(id+"F11.wireOp",EDGE,"E14"),sQuery(id+"F11.wireOp",EDGE,"E16.0"),sQuery(id+"F11.wireOp",EDGE,"E18.0")])]}),"instanceName":"3"});
            var Q4;
            Q4=makeQuery(id+"F15.opPattern","COPY",BODY,{"derivedFrom":makeQuery(id+"F13.opExtrude","SWEPT_BODY",BODY,{"disambiguationData":[OSD([sQuery(id+"F11.wireOp",EDGE,"E13"),sQuery(id+"F11.wireOp",EDGE,"E14"),sQuery(id+"F11.wireOp",EDGE,"E16.0"),sQuery(id+"F11.wireOp",EDGE,"E18.0")])]}),"instanceName":"4"});
            var Q5;
            Q5=makeQuery(id+"F15.opPattern","COPY",BODY,{"derivedFrom":makeQuery(id+"F13.opExtrude","SWEPT_BODY",BODY,{"disambiguationData":[OSD([sQuery(id+"F11.wireOp",EDGE,"E13"),sQuery(id+"F11.wireOp",EDGE,"E14"),sQuery(id+"F11.wireOp",EDGE,"E16.0"),sQuery(id+"F11.wireOp",EDGE,"E18.0")])]}),"instanceName":"5"});
            var Q6;
            Q6=makeQuery(id+"F8.opExtrude","SWEPT_BODY",BODY,{"disambiguationData":[OSD([sQuery(id+"F4.wireOp",EDGE,"E10")])]});
            booleanBodies(context, id + "F16", {"operationType" : BooleanOperationType.SUBTRACTION, "tools" : qUnion([Q0, Q1, Q2, Q3, Q4, Q5]), "targets" : qUnion([Q6])});
        }
    });
